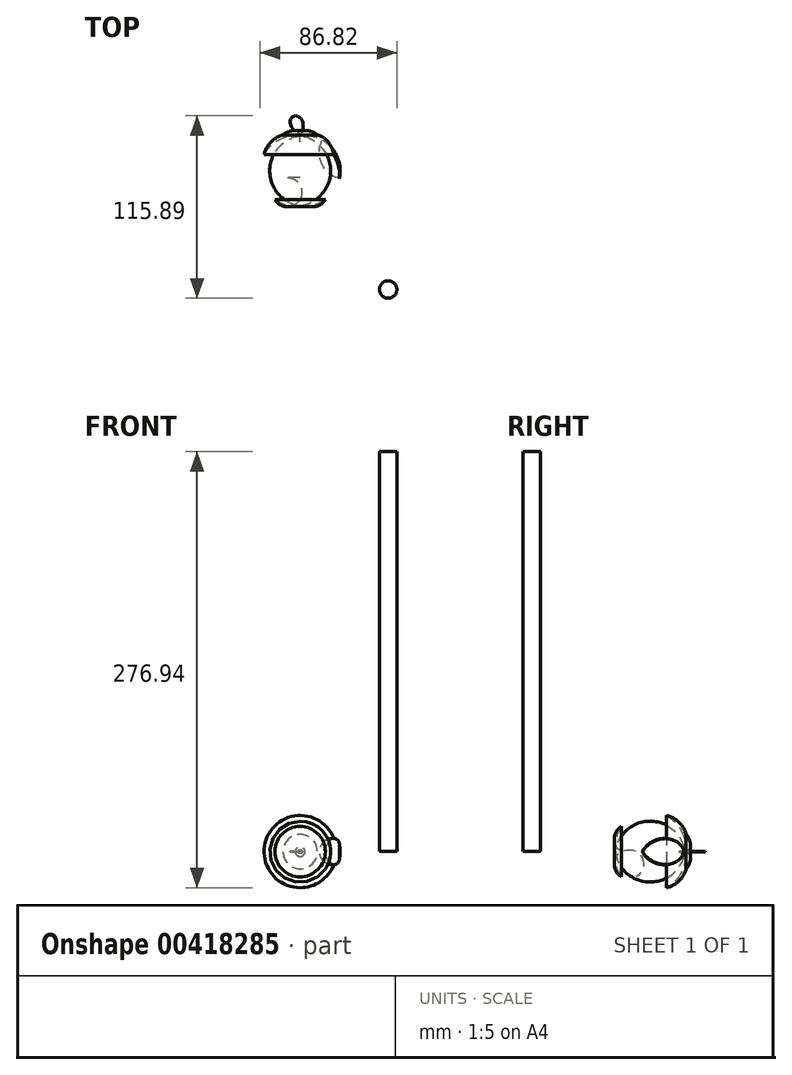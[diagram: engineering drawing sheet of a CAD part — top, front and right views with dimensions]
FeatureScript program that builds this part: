
annotation { "Feature Type Name" : "Feature", "Feature Type Description" : "" }
export const myFeature = defineFeature(function(context is Context, id is Id, definition is map)
    precondition{}
    {
        {
            var Q0;
            Q0=qCreatedBy(makeId("Top.planeOp"),FACE);
            var sketch = newSketch(context, id + "F0", { "sketchPlane" : qUnion([Q0])});
            skArc(sketch, "E0", {"start": v(0, 0) * mm, "mid": v(8, -4.58) * mm, "end": v(16, 0) * mm});
            skArc(sketch, "E1", {"start": v(10.92, 41.07) * mm, "mid": v(7.3, 43.25) * mm, "end": v(3.1, 43.77) * mm});
            skArc(sketch, "E2", {"start": v(3.1, 43.77) * mm, "mid": v(1.28, 42.73) * mm, "end": v(0, 41.07) * mm});
            skLineSegment(sketch, "E3", {"start": v(0, 0) * mm, "end": v(0, 41.07) * mm});
            skArc(sketch, "E4", {"start": v(22.94, 28.45) * mm, "mid": v(18.71, 36.46) * mm, "end": v(10.92, 41.07) * mm});
            skArc(sketch, "E5", {"start": v(16, 0) * mm, "mid": v(24.77, 12.93) * mm, "end": v(22.94, 28.45) * mm});
            skSolve(sketch);
        }
        {
            var Q0;
            Q0=makeQuery(id+"F0.imprint","IMPRINT",FACE,{"disambiguationData":[TD([[makeQuery(id+"F0.imprint","IMPRINT",EDGE,{"derivedFrom":sQuery(id+"F0.wireOp",EDGE,"E0")}),1.0]])]});
            var Q1;
            Q1=sQuery(id+"F0.wireOp",EDGE,"E3");
            revolve(context, id + "F1", {"entities" : qUnion([Q0]), "axis" : qUnion([Q1]), "revolveType" : RevolveType.FULL});
        }
        {
            var Q0;
            Q0=qCreatedBy(makeId("Top.planeOp"),FACE);
            var sketch = newSketch(context, id + "F2", { "sketchPlane" : qUnion([Q0])});
            skFitSpline(sketch, "E6", {"points": [v(0, 41.43) * mm, v(-5.16, 45.7) * mm, v(-6.22, 50.5) * mm, v(-3.73, 53.16) * mm, v(0, 51.92) * mm, v(1.96, 47.12) * mm, v(0, 41.43) * mm]});
            skSolve(sketch);
        }
        {
            var Q0;
            Q0=makeQuery(id+"F2.imprint","IMPRINT",FACE,{"disambiguationData":[TD([[makeQuery(id+"F2.imprint","IMPRINT",EDGE,{"derivedFrom":sQuery(id+"F2.wireOp",EDGE,"E6")}),-1.0]])]});
            extrude(context, id + "F3", {"entities" : qUnion([Q0]), "operationType" : NewBodyOperationType.ADD, "endBound" : BoundingType.SYMMETRIC, "depth" : 0.5 * mm});
        }
        {
            var Q0;
            Q0=qCreatedBy(makeId("Top.planeOp"),FACE);
            var sketch = newSketch(context, id + "F4", { "sketchPlane" : qUnion([Q0])});
            skLineSegment(sketch, "E7", {"start": v(25.43, 13.34) * mm, "end": v(16.36, 41.25) * mm});
            skArc(sketch, "E8", {"start": v(16.36, 41.25) * mm, "mid": v(13, 24.73) * mm, "end": v(25.43, 13.34) * mm});
            skSolve(sketch);
        }
        {
            var Q0;
            Q0 = qSketchRegion(id + "F4", true);
            var Q1;
            Q1=sQuery(id+"F4.wireOp",EDGE,"E7");
            revolve(context, id + "F5", {"operationType" : NewBodyOperationType.REMOVE, "entities" : qUnion([Q0]), "axis" : qUnion([Q1]), "revolveType" : RevolveType.FULL, "oppositeDirection" : true});
        }
        {
            var Q0;
            Q0=qCreatedBy(makeId("Top.planeOp"),FACE);
            var sketch = newSketch(context, id + "F6", { "sketchPlane" : qUnion([Q0])});
            skCircle(sketch, "E9", {"center": v(55.87, -57.1) * mm, "radius": 5.54 * mm});
            skSolve(sketch);
        }
        {
            var Q0;
            Q0=makeQuery(id+"F6.imprint","IMPRINT",FACE,{"disambiguationData":[TD([[makeQuery(id+"F6.imprint","IMPRINT",EDGE,{"derivedFrom":sQuery(id+"F6.wireOp",EDGE,"E9")}),1.0]])]});
            extrude(context, id + "F7", {"entities" : qUnion([Q0]), "depth" : 254 * mm});
        }
    });
